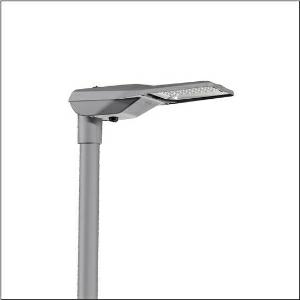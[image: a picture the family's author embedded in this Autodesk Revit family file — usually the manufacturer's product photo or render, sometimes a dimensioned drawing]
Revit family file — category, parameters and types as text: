
# Revit family: streetlight_sl_21_mini___pl52_5xe2h33t08gb_c028
name_source: partatom
category: Lighting Fixtures
units: mm (PartAtom-declared; Revit-internal decimal feet)

## family parameters
Cut with Voids When Loaded = No
Host = Face
Light Source = No
Part Type = Normal
Room Calculation Point = No
Round Connector Dimension = Use Diameter
Shared = No

## types (1)
- --- (1 x LED, 5840 lm, 40.4 W, 3000K)
    Apparent Load = 40 VA
    CIE Flux Codes = 27 59 98 100 100
    Color Rendering = 70
    Color Temperature = 3000K
    Default Elevation = 1800 mm
    Description = Streetlight SL 21 mini, mast luminaire, primary light control with lens, of PMMA, primary optical cover: cover, of toughened safety glass, transparent, light distribution: PL52, light emission: direct distribution, primary light characteristic: asymmetric, installation type: side-entry, post-top, LED, High Power LED, rated luminous flux: 5.840lm, luminous efficacy: 145lm/W, light colour: 730, colour temperature: 3000K, control gear: D4i, control: overheat protection, constant luminous flux control, time-dependent luminous flux control, flexible luminous flux parameterisation, pre-setting: logarithmic dimming characteristic, mains connection: 220..240V, AC, 50/60Hz, start of lifetime: 40W, end of service life: 41W, reduction: 19W, luminaire housing, of diecast aluminium, powder-coated, SITECO metallic grey (DB 702S), corrosivity category C5 high according to DIN EN ISO 12944, please order mast flange separately, inclination adjustable: 0°, 5°, 10°, 15°, sealing non-destructively replaceable, multi-level sealing system, length: 628mm, width: 235mm, height: 110mm, mast flange for spigot size: 42mm (side-entry): 5XC10008XM4, 60/48mm (side-entry/post-top): 5XC10108XM2, 76/60mm (side-entry/post-top): 5XC10108XM1, mounting height: 4..8m, Smart Interface below and above, protection rating (complete): IP66, insulation class (complete): insulation class II (safety insulation), certification: CE, ENEC, ENEC+, VDE, impact resistance: IK10, permissible operating ambient temperature for outdoor applications: -40..+50°C, standard-compliant lighting for roads and squares, packaging unit: 1 piece

Light Distribution: PL52
    Height = 110 mm
    Lamp = 1 x LED
    Lamp Light Flux = 5840 lm
    Lamp Power = 40.4 W
    Lamp count = 1
    Length = 625 mm
    Luminous efficacy = 145 lm/W
    Manufacturer = Siteco
    ModVariant = No
    Model = 5XE2H33T08GB
    Number of Poles = 1
    OnlyDefault = Yes
    Power Factor = 1
    Product Name = Streetlight SL 21 mini | PL52
    Product group = mast luminaire | pylon top
    ProductGroupID = 6100
    Protection Class = Protection class II
    Protection Degree = IP 66
    RLX_Detail_Level = 1
    RLX_Emergency_Light_Flux = 0 lm
    RLX_Emergency_Type = 0
    RLX_Emergency_Type_DB = No
    RlxData = <blob elided: 35929 chars, md5=f79b8bd9>
    Socket = socket
    Standby Power = 0 W
    System Light Flux = 5840 lm
    System Power = 40 W
    Type Comments = factory setting: luminous flux: 100 % | dim-lin: 254 | 812 mA
    Type Image = l_1003514.jpg
    URL = http://relux.com
    VarID = @adj_187521
    Voltage = 0 V
    Weight = 0.00 kg
    Width = 234 mm

## geometry (parser evidence)
native form markers: Blend x4, Sweep x8
no freeform markers — native parametric forms only
